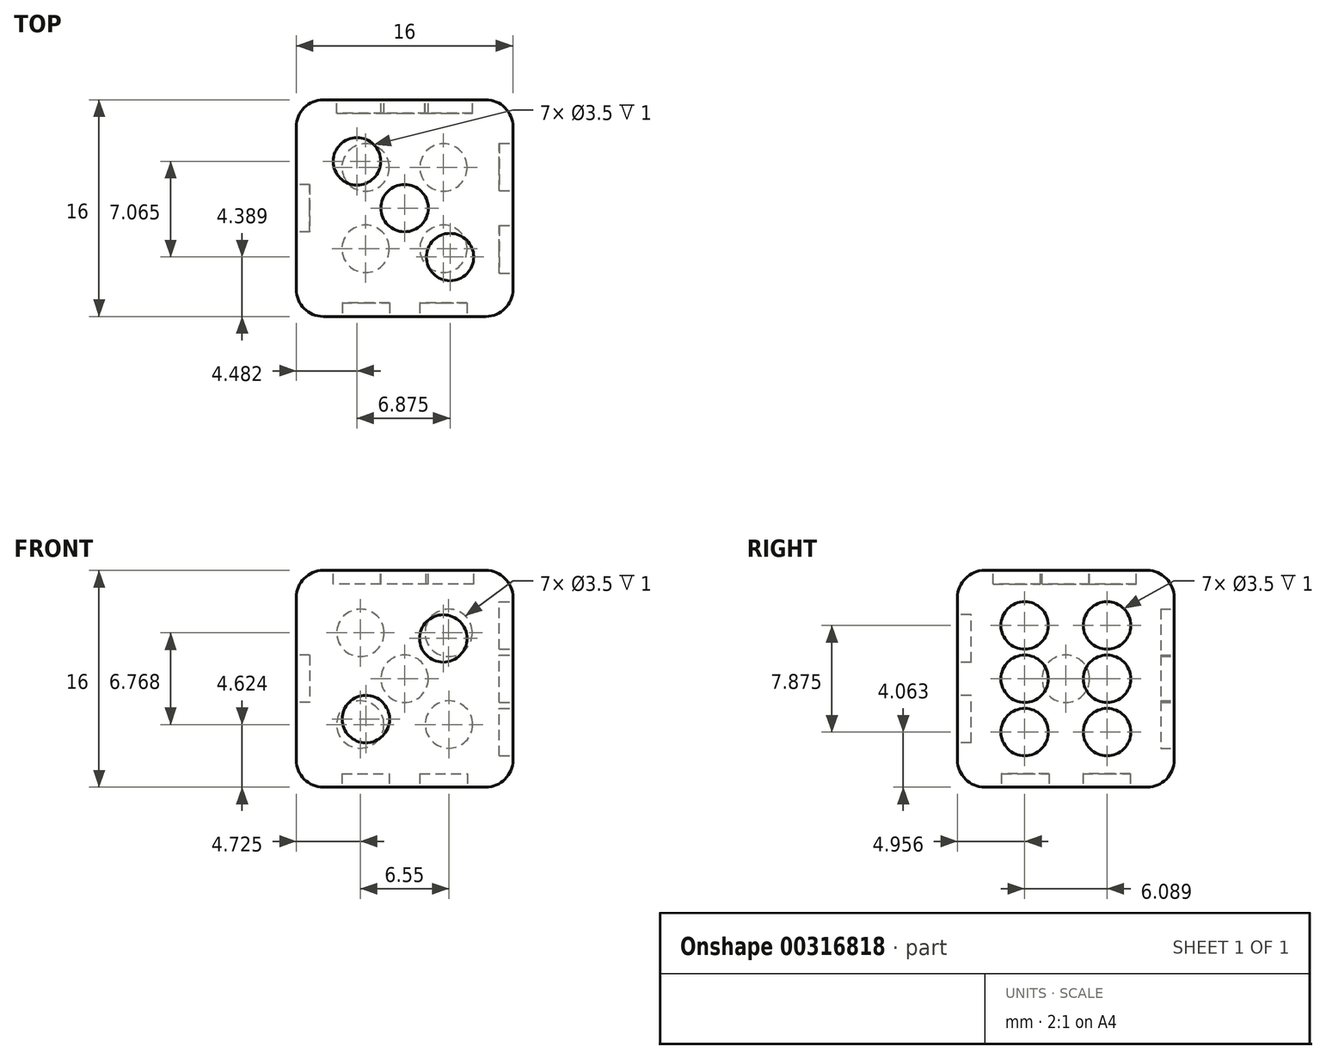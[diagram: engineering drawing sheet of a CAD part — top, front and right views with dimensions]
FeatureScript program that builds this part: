
annotation { "Feature Type Name" : "Feature", "Feature Type Description" : "" }
export const myFeature = defineFeature(function(context is Context, id is Id, definition is map)
    precondition{}
    {
        {
            var Q0;
            Q0=qCreatedBy(makeId("Front.planeOp"),FACE);
            var sketch = newSketch(context, id + "F0", { "sketchPlane" : qUnion([Q0])});
            skLineSegment(sketch, "E0.bottom", {"start": v(8, -8) * mm, "end": v(-8, -8) * mm});
            skLineSegment(sketch, "E0.top", {"start": v(8, 8) * mm, "end": v(-8, 8) * mm});
            skLineSegment(sketch, "E0.left", {"start": v(8, -8) * mm, "end": v(8, 8) * mm});
            skLineSegment(sketch, "E0.right", {"start": v(-8, -8) * mm, "end": v(-8, 8) * mm});
            skPoint(sketch, "E0.middle", {"position": v(0, 0) * mm});
            skSolve(sketch);
        }
        {
            var Q0;
            Q0 = qSketchRegion(id + "F0", true);
            extrude(context, id + "F1", {"entities" : qUnion([Q0]), "endBound" : BoundingType.SYMMETRIC, "depth" : 16 * mm});
        }
        {
            var Q0;
            Q0=makeQuery(id+"F1.opExtrude","CAP_EDGE",EDGE,{"disambiguationData":[OSD([sQuery(id+"F0.wireOp",EDGE,"E0.top")])],"isStart":false});
            var Q1;
            Q1=makeQuery(id+"F1.opExtrude","SWEPT_EDGE",EDGE,{"disambiguationData":[OSD([sQuery(id+"F0.wireOp",EDGE,"E0.top"),sQuery(id+"F0.wireOp",EDGE,"E0.left")])]});
            var Q2;
            Q2=makeQuery(id+"F1.opExtrude","CAP_EDGE",EDGE,{"disambiguationData":[OSD([sQuery(id+"F0.wireOp",EDGE,"E0.top")])],"isStart":true});
            var Q3;
            Q3=makeQuery(id+"F1.opExtrude","SWEPT_EDGE",EDGE,{"disambiguationData":[OSD([sQuery(id+"F0.wireOp",EDGE,"E0.top"),sQuery(id+"F0.wireOp",EDGE,"E0.right")])]});
            var Q4;
            Q4=makeQuery(id+"F1.opExtrude","CAP_EDGE",EDGE,{"disambiguationData":[OSD([sQuery(id+"F0.wireOp",EDGE,"E0.right")])],"isStart":true});
            var Q5;
            Q5=makeQuery(id+"F1.opExtrude","CAP_EDGE",EDGE,{"disambiguationData":[OSD([sQuery(id+"F0.wireOp",EDGE,"E0.right")])],"isStart":false});
            var Q6;
            Q6=makeQuery(id+"F1.opExtrude","SWEPT_EDGE",EDGE,{"disambiguationData":[OSD([sQuery(id+"F0.wireOp",EDGE,"E0.bottom"),sQuery(id+"F0.wireOp",EDGE,"E0.right")])]});
            var Q7;
            Q7=makeQuery(id+"F1.opExtrude","CAP_EDGE",EDGE,{"disambiguationData":[OSD([sQuery(id+"F0.wireOp",EDGE,"E0.bottom")])],"isStart":false});
            var Q8;
            Q8=makeQuery(id+"F1.opExtrude","SWEPT_EDGE",EDGE,{"disambiguationData":[OSD([sQuery(id+"F0.wireOp",EDGE,"E0.bottom"),sQuery(id+"F0.wireOp",EDGE,"E0.left")])]});
            var Q9;
            Q9=makeQuery(id+"F1.opExtrude","CAP_EDGE",EDGE,{"disambiguationData":[OSD([sQuery(id+"F0.wireOp",EDGE,"E0.left")])],"isStart":false});
            var Q10;
            Q10=makeQuery(id+"F1.opExtrude","CAP_EDGE",EDGE,{"disambiguationData":[OSD([sQuery(id+"F0.wireOp",EDGE,"E0.bottom")])],"isStart":true});
            var Q11;
            Q11=makeQuery(id+"F1.opExtrude","CAP_EDGE",EDGE,{"disambiguationData":[OSD([sQuery(id+"F0.wireOp",EDGE,"E0.left")])],"isStart":true});
            fillet(context, id + "F2", {"entities" : qUnion([Q0, Q1, Q2, Q3, Q4, Q5, Q6, Q7, Q8, Q9, Q10, Q11]), "radius" : 2 * mm, "tangentPropagation" : true, "allowEdgeOverflow" : false});
        }
        {
            var Q0;
            Q0=makeQuery(id+"F1.opExtrude","CAP_FACE",FACE,{"disambiguationData":[OSD([sQuery(id+"F0.wireOp",EDGE,"E0.bottom"),sQuery(id+"F0.wireOp",EDGE,"E0.top"),sQuery(id+"F0.wireOp",EDGE,"E0.left"),sQuery(id+"F0.wireOp",EDGE,"E0.right")])],"isStart":false});
            var sketch = newSketch(context, id + "F3", { "sketchPlane" : qUnion([Q0])});
            skCircle(sketch, "E1", {"center": v(2.86, 2.98) * mm, "radius": 1.75 * mm});
            skCircle(sketch, "E2", {"center": v(-2.86, -2.98) * mm, "radius": 1.75 * mm});
            skSolve(sketch);
        }
        {
            var Q0;
            Q0 = qSketchRegion(id + "F3", true);
            extrude(context, id + "F4", {"entities" : qUnion([Q0]), "operationType" : NewBodyOperationType.REMOVE, "oppositeDirection" : true, "depth" : 1 * mm});
        }
        {
            var Q0;
            Q0=makeQuery(id+"F1.opExtrude","SWEPT_FACE",FACE,{"disambiguationData":[OSD([sQuery(id+"F0.wireOp",EDGE,"E0.top")])]});
            var sketch = newSketch(context, id + "F5", { "sketchPlane" : qUnion([Q0])});
            skCircle(sketch, "E3", {"center": v(0, 0) * mm, "radius": 1.75 * mm});
            skCircle(sketch, "E4", {"center": v(-3.52, 3.45) * mm, "radius": 1.75 * mm});
            skCircle(sketch, "E5", {"center": v(3.36, -3.61) * mm, "radius": 1.75 * mm});
            skSolve(sketch);
        }
        {
            var Q0;
            Q0 = qSketchRegion(id + "F5", true);
            extrude(context, id + "F6", {"entities" : qUnion([Q0]), "operationType" : NewBodyOperationType.REMOVE, "oppositeDirection" : true, "depth" : 1 * mm});
        }
        {
            var Q0;
            Q0=makeQuery(id+"F1.opExtrude","SWEPT_FACE",FACE,{"disambiguationData":[OSD([sQuery(id+"F0.wireOp",EDGE,"E0.left")])]});
            var sketch = newSketch(context, id + "F7", { "sketchPlane" : qUnion([Q0])});
            skCircle(sketch, "E6", {"center": v(3.04, 0) * mm, "radius": 1.75 * mm});
            skCircle(sketch, "E7", {"center": v(-3.04, 0) * mm, "radius": 1.75 * mm});
            skCircle(sketch, "E8", {"center": v(-3.04, 3.94) * mm, "radius": 1.75 * mm});
            skCircle(sketch, "E9", {"center": v(3.04, 3.94) * mm, "radius": 1.75 * mm});
            skCircle(sketch, "E10", {"center": v(-3.04, -3.94) * mm, "radius": 1.75 * mm});
            skCircle(sketch, "E11", {"center": v(3.04, -3.94) * mm, "radius": 1.75 * mm});
            skSolve(sketch);
        }
        {
            var Q0;
            Q0 = qSketchRegion(id + "F7", true);
            extrude(context, id + "F8", {"entities" : qUnion([Q0]), "operationType" : NewBodyOperationType.REMOVE, "oppositeDirection" : true, "depth" : 1 * mm});
        }
        {
            var Q0;
            Q0=makeQuery(id+"F1.opExtrude","CAP_FACE",FACE,{"disambiguationData":[OSD([sQuery(id+"F0.wireOp",EDGE,"E0.bottom"),sQuery(id+"F0.wireOp",EDGE,"E0.top"),sQuery(id+"F0.wireOp",EDGE,"E0.left"),sQuery(id+"F0.wireOp",EDGE,"E0.right")])],"isStart":true});
            var sketch = newSketch(context, id + "F9", { "sketchPlane" : qUnion([Q0])});
            skCircle(sketch, "E12", {"center": v(0, 0) * mm, "radius": 1.75 * mm});
            skCircle(sketch, "E13", {"center": v(-3.26, 3.4) * mm, "radius": 1.75 * mm});
            skCircle(sketch, "E14", {"center": v(3.26, 3.4) * mm, "radius": 1.75 * mm});
            skCircle(sketch, "E15", {"center": v(-3.28, -3.38) * mm, "radius": 1.75 * mm});
            skCircle(sketch, "E16", {"center": v(3.28, -3.38) * mm, "radius": 1.75 * mm});
            skSolve(sketch);
        }
        {
            var Q0;
            Q0 = qSketchRegion(id + "F9", true);
            extrude(context, id + "F10", {"entities" : qUnion([Q0]), "operationType" : NewBodyOperationType.REMOVE, "oppositeDirection" : true, "depth" : 1 * mm});
        }
        {
            var Q0;
            Q0=makeQuery(id+"F1.opExtrude","SWEPT_FACE",FACE,{"disambiguationData":[OSD([sQuery(id+"F0.wireOp",EDGE,"E0.bottom")])]});
            var sketch = newSketch(context, id + "F11", { "sketchPlane" : qUnion([Q0])});
            skCircle(sketch, "E17", {"center": v(2.88, -3) * mm, "radius": 1.75 * mm});
            skCircle(sketch, "E18", {"center": v(-2.88, -3) * mm, "radius": 1.75 * mm});
            skCircle(sketch, "E19", {"center": v(2.88, 3) * mm, "radius": 1.75 * mm});
            skCircle(sketch, "E20", {"center": v(-2.88, 3) * mm, "radius": 1.75 * mm});
            skSolve(sketch);
        }
        {
            var Q0;
            Q0 = qSketchRegion(id + "F11", true);
            extrude(context, id + "F12", {"entities" : qUnion([Q0]), "operationType" : NewBodyOperationType.REMOVE, "oppositeDirection" : true, "depth" : 1 * mm});
        }
        {
            var Q0;
            Q0=makeQuery(id+"F1.opExtrude","SWEPT_FACE",FACE,{"disambiguationData":[OSD([sQuery(id+"F0.wireOp",EDGE,"E0.right")])]});
            var sketch = newSketch(context, id + "F13", { "sketchPlane" : qUnion([Q0])});
            skCircle(sketch, "E21", {"center": v(0, 0) * mm, "radius": 1.75 * mm});
            skSolve(sketch);
        }
        {
            var Q0;
            Q0 = qSketchRegion(id + "F13", true);
            extrude(context, id + "F14", {"entities" : qUnion([Q0]), "operationType" : NewBodyOperationType.REMOVE, "oppositeDirection" : true, "depth" : 1 * mm});
        }
    });
